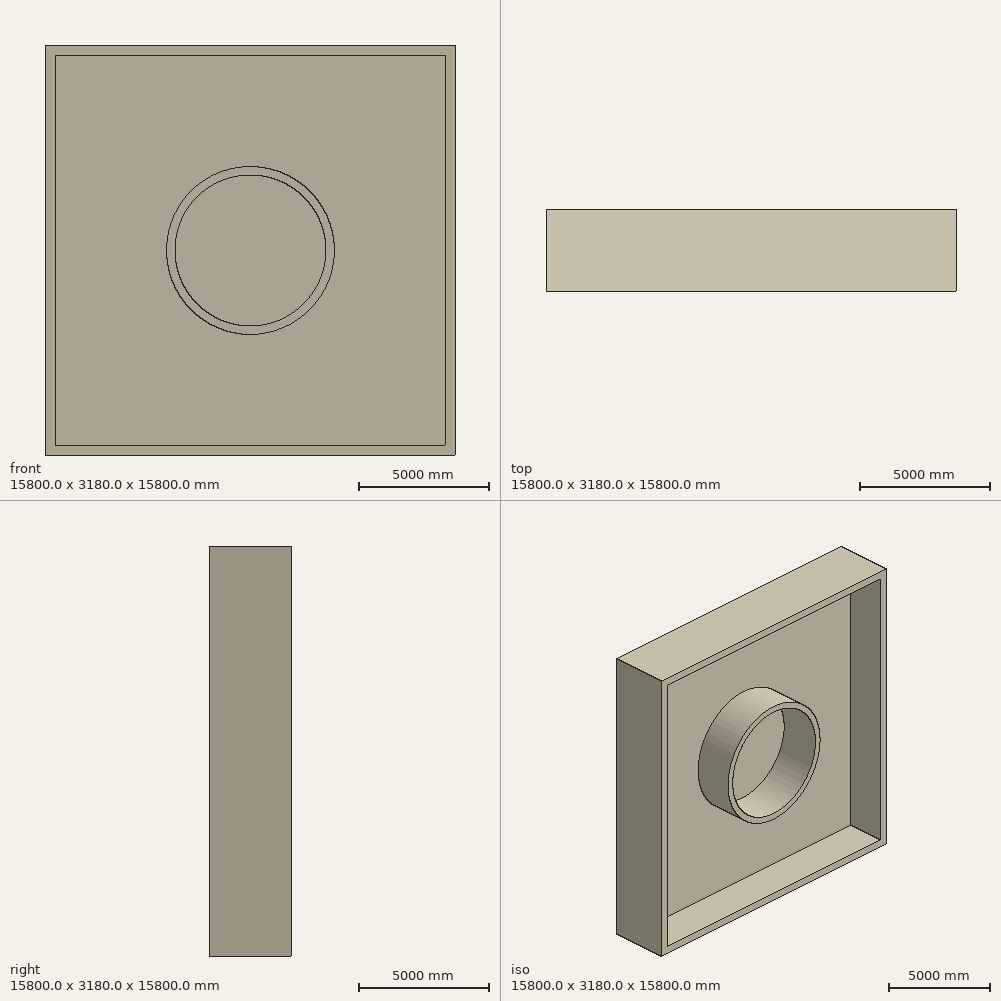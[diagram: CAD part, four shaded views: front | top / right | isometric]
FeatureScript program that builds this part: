
annotation { "Feature Type Name" : "Feature", "Feature Type Description" : "" }
export const myFeature = defineFeature(function(context is Context, id is Id, definition is map)
    precondition{}
    {
        {
            var Q0;
            Q0=qCreatedBy(makeId("Front.planeOp"),FACE);
            var sketch = newSketch(context, id + "F0", { "sketchPlane" : qUnion([Q0])});
            skLineSegment(sketch, "E0.bottom", {"start": v(7900, -7900) * mm, "end": v(-7900, -7900) * mm});
            skLineSegment(sketch, "E0.top", {"start": v(7900, 7900) * mm, "end": v(-7900, 7900) * mm});
            skLineSegment(sketch, "E0.left", {"start": v(7900, -7900) * mm, "end": v(7900, 7900) * mm});
            skLineSegment(sketch, "E0.right", {"start": v(-7900, -7900) * mm, "end": v(-7900, 7900) * mm});
            skPoint(sketch, "E0.middle", {"position": v(0, 0) * mm});
            skSolve(sketch);
        }
        {
            var Q0;
            Q0 = qSketchRegion(id + "F0", true);
            extrude(context, id + "F1", {"entities" : qUnion([Q0]), "depth" : 3.18 * 1000 * mm});
        }
        {
            var Q0;
            Q0=makeQuery(id+"F1.opExtrude","CAP_FACE",FACE,{"disambiguationData":[OSD([sQuery(id+"F0.wireOp",EDGE,"E0.bottom"),sQuery(id+"F0.wireOp",EDGE,"E0.top"),sQuery(id+"F0.wireOp",EDGE,"E0.left"),sQuery(id+"F0.wireOp",EDGE,"E0.right")])],"isStart":false});
            var sketch = newSketch(context, id + "F2", { "sketchPlane" : qUnion([Q0])});
            skCircle(sketch, "E1", {"center": v(0, 0) * mm, "radius": 3235 * mm});
            skSolve(sketch);
        }
        {
            var Q0;
            Q0=makeQuery(id+"F2.imprint","IMPRINT",FACE,{"disambiguationData":[TD([[makeQuery(id+"F2.imprint","IMPRINT",EDGE,{"derivedFrom":sQuery(id+"F2.wireOp",EDGE,"E1")}),-1.0]])]});
            var sketch = newSketch(context, id + "F3", { "sketchPlane" : qUnion([Q0])});
            skLineSegment(sketch, "E2.bottom", {"start": v(7500, -7500) * mm, "end": v(-7500, -7500) * mm});
            skLineSegment(sketch, "E2.top", {"start": v(7500, 7500) * mm, "end": v(-7500, 7500) * mm});
            skLineSegment(sketch, "E2.left", {"start": v(7500, -7500) * mm, "end": v(7500, 7500) * mm});
            skLineSegment(sketch, "E2.right", {"start": v(-7500, -7500) * mm, "end": v(-7500, 7500) * mm});
            skPoint(sketch, "E2.middle", {"position": v(0, 0) * mm});
            skSolve(sketch);
        }
        {
            var Q0;
            Q0 = qSketchRegion(id + "F3", true);
            extrude(context, id + "F4", {"entities" : qUnion([Q0]), "operationType" : NewBodyOperationType.REMOVE, "oppositeDirection" : true, "depth" : 2100 * mm});
        }
        {
            var Q0;
            Q0=makeQuery(id+"F2.imprint","IMPRINT",FACE,{"disambiguationData":[TD([[makeQuery(id+"F2.imprint","IMPRINT",EDGE,{"derivedFrom":sQuery(id+"F2.wireOp",EDGE,"E1")}),1.0]])]});
            var Q1;
            Q1=sQuery(id+"F2.wireOp",EDGE,"E1");
            extrude(context, id + "F5", {"entities" : qUnion([Q0]), "operationType" : NewBodyOperationType.ADD, "surfaceEntities" : qUnion([Q1]), "endBound" : BoundingType.UP_TO_NEXT, "oppositeDirection" : true, "depth" : 2159.1 * mm});
        }
        {
            var Q0;
            Q0=makeQuery(id+"F5.opExtrude","CAP_FACE",FACE,{"disambiguationData":[OSD([sQuery(id+"F2.wireOp",EDGE,"E1")])],"isStart":true});
            var sketch = newSketch(context, id + "F6", { "sketchPlane" : qUnion([Q0])});
            skCircle(sketch, "E3", {"center": v(0, 0) * mm, "radius": 2910 * mm});
            skSolve(sketch);
        }
        {
            var Q0;
            Q0 = qSketchRegion(id + "F6", true);
            extrude(context, id + "F7", {"entities" : qUnion([Q0]), "operationType" : NewBodyOperationType.REMOVE, "oppositeDirection" : true, "depth" : 2200 * mm});
        }
    });
